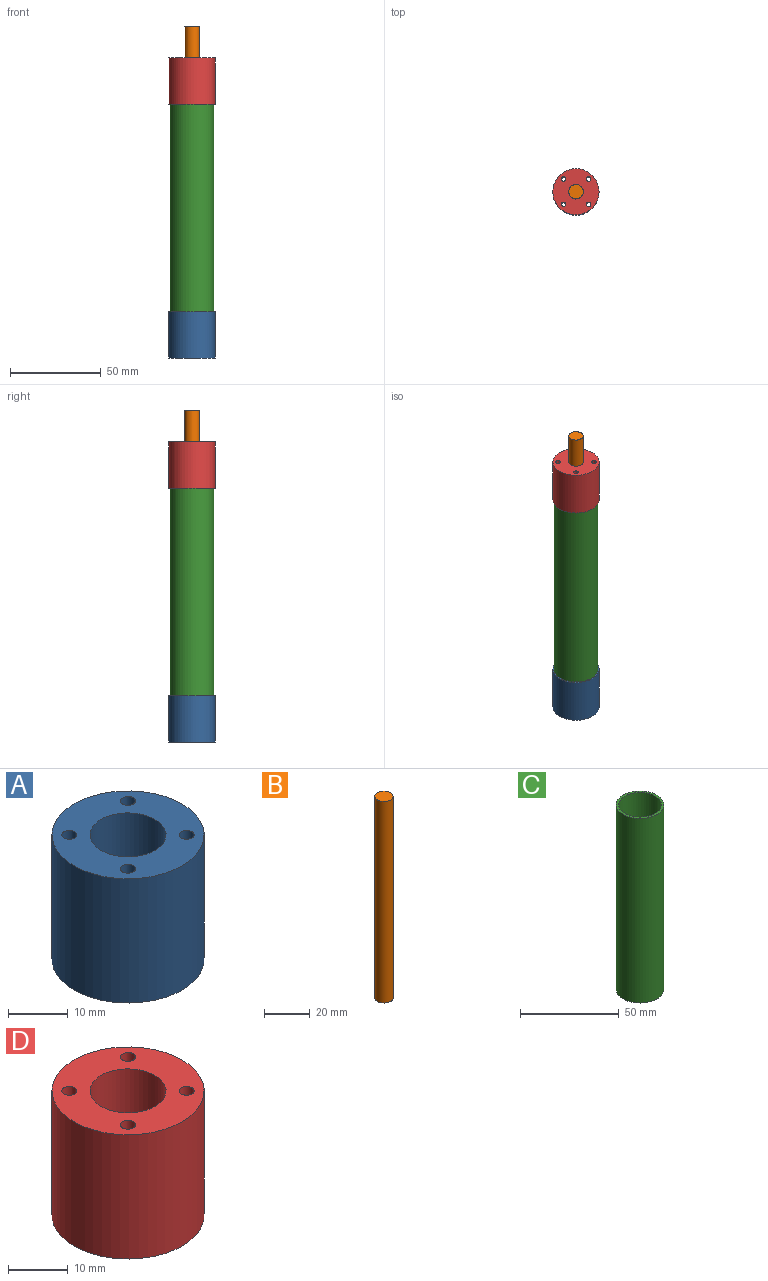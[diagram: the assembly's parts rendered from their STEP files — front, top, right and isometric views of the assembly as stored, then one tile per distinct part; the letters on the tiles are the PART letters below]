
ASSEMBLY  parts=4 mates=3
PART A: 10 faces, bbox 25.4x25.4x25.4 mm
  f0: cylinder r=6.35mm len=17.78mm, axis (0,0,-1), area 709.4mm2, adj f6,f9
  f1: cylinder r=1.27mm len=25.4mm, axis (0,0,-1), area 202.7mm2, adj f6,f7
  f2: cylinder r=1.27mm len=25.4mm, axis (0,0,-1), area 202.7mm2, adj f6,f7
  f3: cylinder r=1.27mm len=25.4mm, axis (0,0,-1), area 202.7mm2, adj f6,f7
  f4: cylinder r=1.27mm len=25.4mm, axis (0,0,-1), area 202.7mm2, adj f6,f7
  f5: cylinder r=12.7mm len=25.4mm, axis (0,0,-1), area 2026.8mm2, adj f6,f7
  f6: plane 25.4x25.4mm, normal (0,0,1), area 359.8mm2, adj f0,f1,f2,f3,f4,f5
  f7: plane 25.4x25.4mm, normal (0,0,-1), area 436.2mm2, adj f1,f2,f3,f4,f5,f8
  f8: cylinder r=4mm len=8mm, axis (0,0,-1), area 191.5mm2, adj f7,f9
  f9: plane 12.7x12.7mm, normal (0,0,1), area 76.4mm2, adj f0,f8
PART B: 3 faces, bbox 8x8x108 mm
  f0: cylinder r=3.99mm len=107.95mm, axis (0,0,-1), area 2704.8mm2, adj f1,f2
  f1: plane 7.98x7.98mm, normal (0,0,1), area 50mm2, adj f0
  f2: plane 7.98x7.98mm, normal (0,0,-1), area 50mm2, adj f0
PART C: 4 faces, bbox 24.1x24.1x114.3 mm
  f0: cylinder r=10.79mm len=114.3mm, axis (0,0,-1), area 7752.6mm2, adj f2,f3
  f1: cylinder r=12.06mm len=114.3mm, axis (0,0,-1), area 8664.7mm2, adj f2,f3
  f2: plane 24.13x24.13mm, normal (0,0,1), area 91.2mm2, adj f0,f1
  f3: plane 24.13x24.13mm, normal (0,0,-1), area 91.2mm2, adj f0,f1
PART D: 10 faces, bbox 25.4x25.4x25.4 mm
  f0: cylinder r=6.35mm len=17.78mm, axis (0,0,-1), area 709.4mm2, adj f6,f9
  f1: cylinder r=1.27mm len=25.4mm, axis (0,0,-1), area 202.7mm2, adj f6,f7
  f2: cylinder r=1.27mm len=25.4mm, axis (0,0,-1), area 202.7mm2, adj f6,f7
  f3: cylinder r=1.27mm len=25.4mm, axis (0,0,-1), area 202.7mm2, adj f6,f7
  f4: cylinder r=1.27mm len=25.4mm, axis (0,0,-1), area 202.7mm2, adj f6,f7
  f5: cylinder r=12.7mm len=25.4mm, axis (0,0,-1), area 2026.8mm2, adj f6,f7
  f6: plane 25.4x25.4mm, normal (0,0,1), area 359.8mm2, adj f0,f1,f2,f3,f4,f5
  f7: plane 25.4x25.4mm, normal (0,0,-1), area 436.2mm2, adj f1,f2,f3,f4,f5,f8
  f8: cylinder r=4mm len=8mm, axis (0,0,-1), area 191.5mm2, adj f7,f9
  f9: plane 12.7x12.7mm, normal (0,0,1), area 76.4mm2, adj f0,f8
PLACE A t=(-7.26,4.9,29.84)mm
PLACE B t=(-7.45,4.78,104.6)mm
PLACE C t=(-7.45,4.78,55.24)mm fixed
PLACE D rot(axis=(1,0,0),180deg) t=(-7.45,4.78,194.94)mm
MATE slider B.f0 <-> C.f0  axis (0,0,-1) through (-7.45,4.78,104.6)mm
MATE fastened A.f0 <-> C.f0  axis (0,0,1) through (-7.45,4.78,55.24)mm
MATE fastened C.f0 <-> D.f0  axis (0,0,-1) through (-7.45,4.78,169.54)mm
